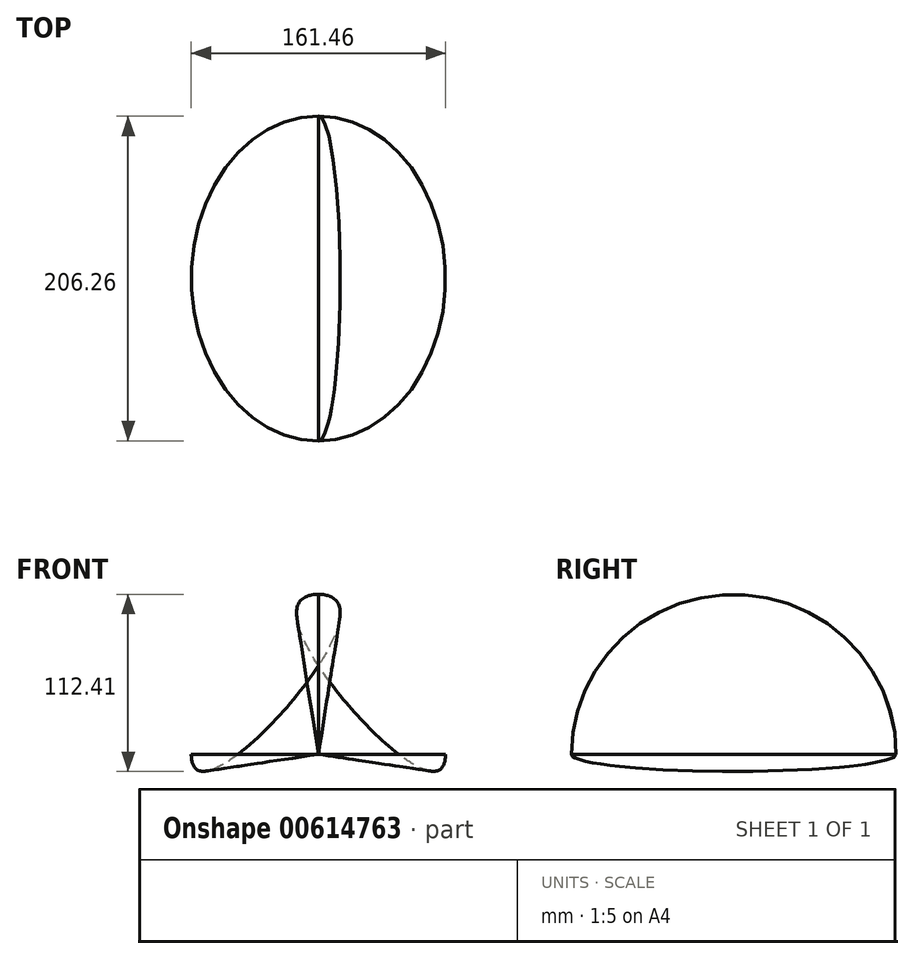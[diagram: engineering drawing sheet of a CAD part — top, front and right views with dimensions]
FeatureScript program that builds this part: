
annotation { "Feature Type Name" : "Feature", "Feature Type Description" : "" }
export const myFeature = defineFeature(function(context is Context, id is Id, definition is map)
    precondition{}
    {
        {
            var Q0;
            Q0=qCreatedBy(makeId("Top.planeOp"),FACE);
            var sketch = newSketch(context, id + "F0", { "sketchPlane" : qUnion([Q0])});
            skEllipticalArc(sketch, "E0", {});
            skLineSegment(sketch, "E1", {"start": v(0, -103.13) * mm, "end": v(0, 103.13) * mm});
            skLineSegment(sketch, "E2", {"start": v(0, 0) * mm, "end": v(-80.73, 0) * mm});
            skPoint(sketch, "E2.endSnap0", {"position": v(-80.73, 0) * mm});
            const initialGuessF0  = {"E0": [0, 0, 0, -1, 0.10313096642494202, 0.0807296552852769, 3.141592653589793, 0]};
            skSetInitialGuess(sketch, initialGuessF0);
            skSolve(sketch);
        }
        {
            var Q0;
            Q0=qCreatedBy(makeId("Right.planeOp"),FACE);
            var sketch = newSketch(context, id + "F1", { "sketchPlane" : qUnion([Q0])});
            skLineSegment(sketch, "E3.0", {"start": v(-103.13, 0) * mm, "end": v(103.13, 0) * mm});
            skEllipticalArc(sketch, "E4", {});
            skLineSegment(sketch, "E5", {"start": v(0, 0) * mm, "end": v(0, 101.6) * mm});
            skPoint(sketch, "E5.endSnap0", {"position": v(0, 101.6) * mm});
            const initialGuessF1  = {"E4": [0, 0, -1, 0, 0.10313096642494202, 0.1016, 3.141592653589793, 0]};
            skSetInitialGuess(sketch, initialGuessF1);
            skSolve(sketch);
        }
        {
            var Q0;
            Q0=sQuery(id+"F0.wireOp",EDGE,"E0");
            var Q1;
            Q1=sQuery(id+"F1.wireOp",EDGE,"E4");
            loft(context, id + "F2", {"bodyType" : ToolBodyType.SURFACE, "startCondition" : LoftEndDerivativeType.NORMAL_TO_PROFILE, "startMagnitude" : -1.5, "endCondition" : LoftEndDerivativeType.NORMAL_TO_PROFILE, "endMagnitude" : -2, "wireProfilesArray" : [{ "wireProfileEntities" : qUnion([Q0]) }, { "wireProfileEntities" : qUnion([Q1]) }]});
        }
        {
            var Q0;
            Q0=makeQuery(id+"F2.opLoft","SWEPT_BODY",BODY,{"disambiguationData":[OSD([sQuery(id+"F0.wireOp",EDGE,"E0"),sQuery(id+"F1.wireOp",EDGE,"E4")])]});
            var Q1;
            Q1=qCreatedBy(makeId("Right.planeOp"),FACE);
            mirror(context, id + "F3", {"entities" : qUnion([Q0]), "mirrorPlane" : qUnion([Q1])});
        }
        {
            var Q0;
            Q0=makeQuery(id+"F2.opLoft","MID_CAP_EDGE",EDGE,{"disambiguationData":[OSD([sQuery(id+"F0.wireOp",VERTEX,"E0.start"),sQuery(id+"F0.wireOp",VERTEX,"E0.end"),sQuery(id+"F0.wireOp",EDGE,"E0")])],"capPos":0.0});
            var Q1;
            Q1=makeQuery(id+"F3.opPattern","COPY",EDGE,{"derivedFrom":makeQuery(id+"F2.opLoft","MID_CAP_EDGE",EDGE,{"disambiguationData":[OSD([sQuery(id+"F0.wireOp",VERTEX,"E0.start"),sQuery(id+"F0.wireOp",VERTEX,"E0.end"),sQuery(id+"F0.wireOp",EDGE,"E0")])],"capPos":0.0}),"instanceName":"1"});
            loft(context, id + "F4", {"bodyType" : ToolBodyType.SURFACE, "wireProfilesArray" : [{ "wireProfileEntities" : qUnion([Q0]) }, { "wireProfileEntities" : qUnion([Q1]) }]});
        }
    });
